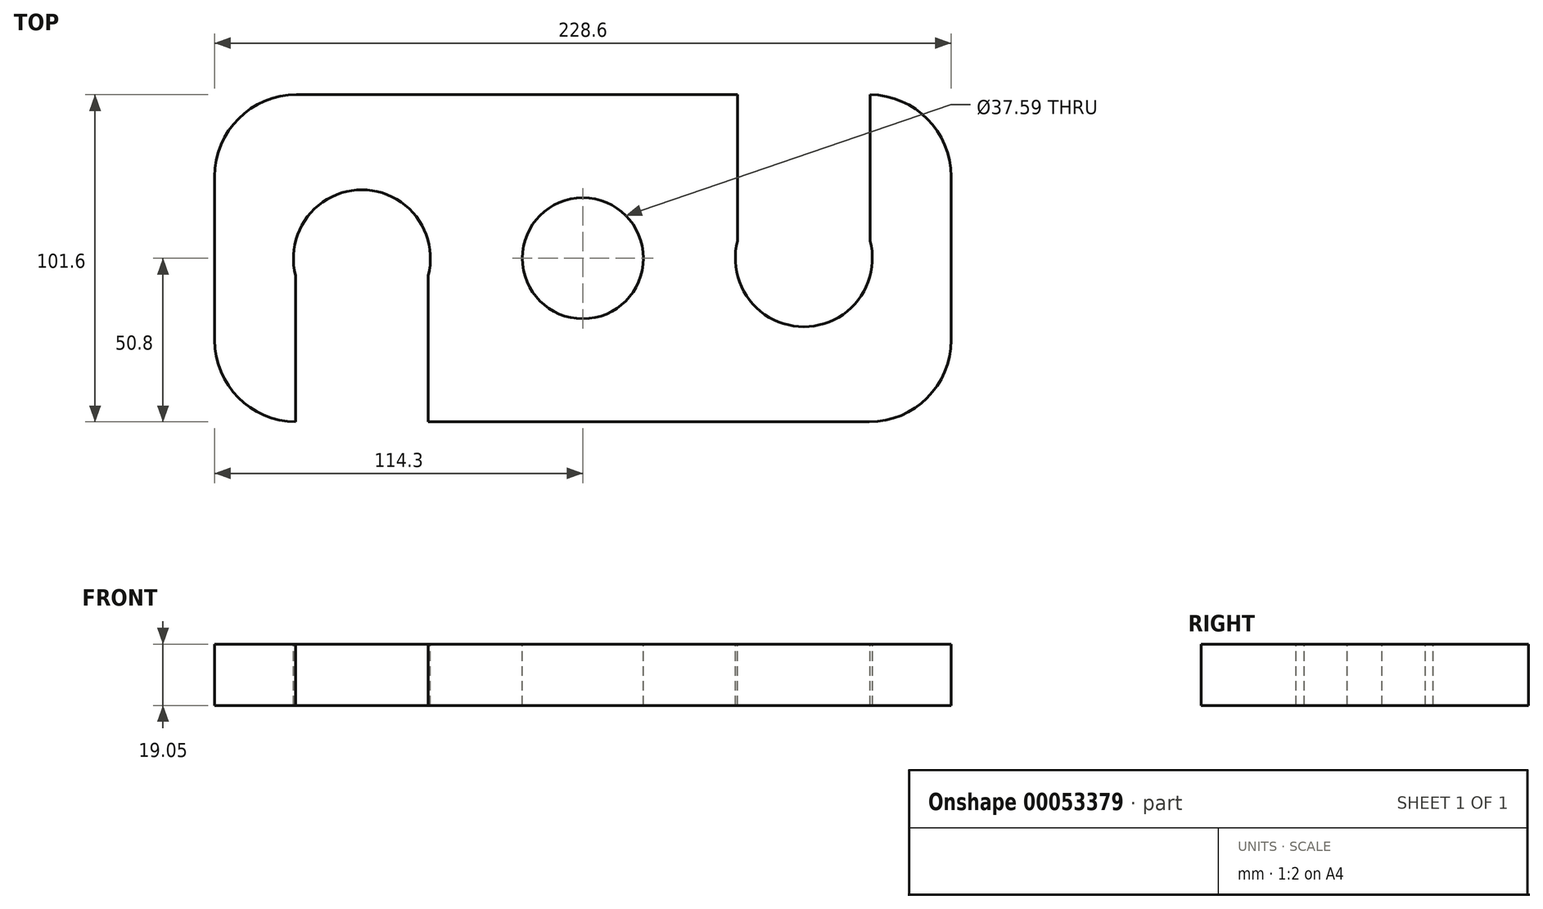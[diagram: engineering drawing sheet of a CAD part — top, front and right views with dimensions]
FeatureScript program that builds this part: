
annotation { "Feature Type Name" : "Feature", "Feature Type Description" : "" }
export const myFeature = defineFeature(function(context is Context, id is Id, definition is map)
    precondition{}
    {
        {
            var Q0;
            Q0=qCreatedBy(makeId("Top.planeOp"),FACE);
            var sketch = newSketch(context, id + "F0", { "sketchPlane" : qUnion([Q0])});
            skLineSegment(sketch, "E0.rect.bottom", {"start": v(88.9, 50.8) * mm, "end": v(-88.9, 50.8) * mm});
            skLineSegment(sketch, "E0.rect.top", {"start": v(88.9, -50.8) * mm, "end": v(-88.9, -50.8) * mm});
            skLineSegment(sketch, "E0.rect.left", {"start": v(114.3, 25.4) * mm, "end": v(114.3, -25.4) * mm});
            skLineSegment(sketch, "E0.rect.right", {"start": v(-114.3, 25.4) * mm, "end": v(-114.3, -25.4) * mm});
            skPoint(sketch, "E0.rect.middle", {"position": v(0, 0) * mm});
            skPoint(sketch, "E1.visualSharp", {"position": v(-114.3, 50.8) * mm});
            skArc(sketch, "E1.filletArc", {"start": v(-88.9, 50.8) * mm, "mid": v(-106.86, 43.36) * mm, "end": v(-114.3, 25.4) * mm});
            skPoint(sketch, "E2.visualSharp", {"position": v(-114.3, -50.8) * mm});
            skArc(sketch, "E2.filletArc", {"start": v(-114.3, -25.4) * mm, "mid": v(-106.86, -43.36) * mm, "end": v(-88.9, -50.8) * mm});
            skPoint(sketch, "E3.visualSharp", {"position": v(114.3, -50.8) * mm});
            skArc(sketch, "E3.filletArc", {"start": v(88.9, -50.8) * mm, "mid": v(106.86, -43.36) * mm, "end": v(114.3, -25.4) * mm});
            skPoint(sketch, "E4.visualSharp", {"position": v(114.3, 50.8) * mm});
            skArc(sketch, "E4.filletArc", {"start": v(114.3, 25.4) * mm, "mid": v(106.86, 43.36) * mm, "end": v(88.9, 50.8) * mm});
            skSolve(sketch);
        }
        {
            var Q0;
            Q0=makeQuery(id+"F0.imprint","IMPRINT",FACE,{"disambiguationData":[TD([[makeQuery(id+"F0.imprint","IMPRINT",EDGE,{"derivedFrom":sQuery(id+"F0.wireOp",EDGE,"E0.rect.bottom")}),1.0]])]});
            extrude(context, id + "F1", {"entities" : qUnion([Q0]), "depth" : 19.05 * mm});
        }
        {
            var Q0;
            Q0=makeQuery(id+"F1.opExtrude","CAP_FACE",FACE,{"disambiguationData":[OSD([sQuery(id+"F0.wireOp",EDGE,"E0.rect.bottom"),sQuery(id+"F0.wireOp",EDGE,"E0.rect.top"),sQuery(id+"F0.wireOp",EDGE,"E0.rect.left"),sQuery(id+"F0.wireOp",EDGE,"E0.rect.right"),sQuery(id+"F0.wireOp",EDGE,"E1.filletArc"),sQuery(id+"F0.wireOp",EDGE,"E2.filletArc"),sQuery(id+"F0.wireOp",EDGE,"E3.filletArc"),sQuery(id+"F0.wireOp",EDGE,"E4.filletArc")])],"isStart":false});
            var sketch = newSketch(context, id + "F2", { "sketchPlane" : qUnion([Q0])});
            skCircle(sketch, "E5", {"center": v(0, 0) * mm, "radius": 18.8 * mm});
            skSolve(sketch);
        }
        {
            var Q0;
            Q0 = qSketchRegion(id + "F2", true);
            extrude(context, id + "F3", {"entities" : qUnion([Q0]), "operationType" : NewBodyOperationType.REMOVE, "endBound" : BoundingType.THROUGH_ALL, "oppositeDirection" : true, "depth" : 25.4 * mm});
        }
        {
            var Q0;
            Q0=makeQuery(id+"F1.opExtrude","CAP_FACE",FACE,{"disambiguationData":[OSD([sQuery(id+"F0.wireOp",EDGE,"E0.rect.bottom"),sQuery(id+"F0.wireOp",EDGE,"E0.rect.top"),sQuery(id+"F0.wireOp",EDGE,"E0.rect.left"),sQuery(id+"F0.wireOp",EDGE,"E0.rect.right"),sQuery(id+"F0.wireOp",EDGE,"E1.filletArc"),sQuery(id+"F0.wireOp",EDGE,"E2.filletArc"),sQuery(id+"F0.wireOp",EDGE,"E3.filletArc"),sQuery(id+"F0.wireOp",EDGE,"E4.filletArc")])],"isStart":false});
            var sketch = newSketch(context, id + "F4", { "sketchPlane" : qUnion([Q0])});
            skArc(sketch, "E6", {"start": v(-48, -5.4) * mm, "mid": v(-68.58, 21.27) * mm, "end": v(-89.15, -5.4) * mm});
            skArc(sketch, "E7.MirrorC", {"start": v(89.15, 5.4) * mm, "mid": v(68.58, -21.27) * mm, "end": v(48, 5.4) * mm});
            skLineSegment(sketch, "E8", {"start": v(-89.15, -50.8) * mm, "end": v(-89.15, -5.4) * mm});
            skLineSegment(sketch, "E9", {"start": v(-48, -50.8) * mm, "end": v(-48, -5.4) * mm});
            skLineSegment(sketch, "E10", {"start": v(89.15, 50.8) * mm, "end": v(89.15, 5.4) * mm});
            skLineSegment(sketch, "E11", {"start": v(48, 50.8) * mm, "end": v(48, 5.4) * mm});
            skLineSegment(sketch, "E12", {"start": v(-89.15, -50.8) * mm, "end": v(-48, -50.8) * mm});
            skLineSegment(sketch, "E13", {"start": v(48, 50.8) * mm, "end": v(89.15, 50.8) * mm});
            skLineSegment(sketch, "E14", {"start": v(-89.15, -5.4) * mm, "end": v(-48, -5.4) * mm, "construction": true});
            skLineSegment(sketch, "E15", {"start": v(48, 5.4) * mm, "end": v(89.15, 5.4) * mm, "construction": true});
            skSolve(sketch);
        }
        {
            var Q0;
            Q0 = qSketchRegion(id + "F4", true);
            extrude(context, id + "F5", {"entities" : qUnion([Q0]), "operationType" : NewBodyOperationType.REMOVE, "endBound" : BoundingType.THROUGH_ALL, "oppositeDirection" : true, "depth" : 25.4 * mm});
        }
    });
